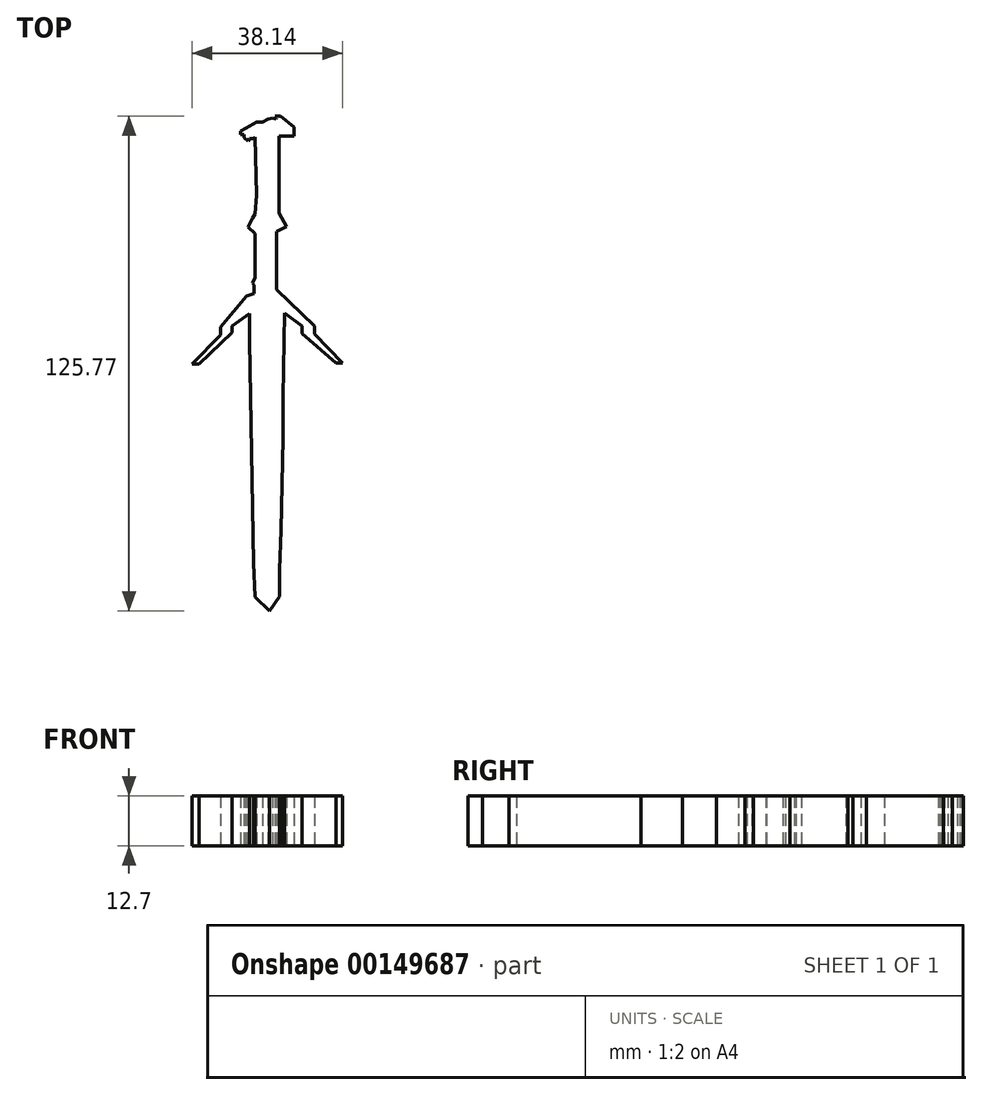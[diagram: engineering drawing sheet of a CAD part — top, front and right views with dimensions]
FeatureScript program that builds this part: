
annotation { "Feature Type Name" : "Feature", "Feature Type Description" : "" }
export const myFeature = defineFeature(function(context is Context, id is Id, definition is map)
    precondition{}
    {
        {
            var Q0;
            Q0=qCreatedBy(makeId("Top.planeOp"),FACE);
            var sketch = newSketch(context, id + "F0", { "sketchPlane" : qUnion([Q0])});
            skLineSegment(sketch, "E0", {"start": v(5, 59.14) * mm, "end": v(8.47, 56.32) * mm});
            skLineSegment(sketch, "E1", {"start": v(8.47, 56.32) * mm, "end": v(8.47, 54.07) * mm});
            skLineSegment(sketch, "E2", {"start": v(8.47, 54.07) * mm, "end": v(4.65, 54.07) * mm});
            skLineSegment(sketch, "E3", {"start": v(4.65, 54.07) * mm, "end": v(4.65, 50.16) * mm});
            skLineSegment(sketch, "E4", {"start": v(4.65, 50.16) * mm, "end": v(4.65, 34.5) * mm});
            skLineSegment(sketch, "E5", {"start": v(4.65, 34.5) * mm, "end": v(6.46, 31.1) * mm});
            skLineSegment(sketch, "E6", {"start": v(6.46, 31.1) * mm, "end": v(4.01, 29.8) * mm});
            skLineSegment(sketch, "E7", {"start": v(4.01, 29.8) * mm, "end": v(4.01, 15.05) * mm});
            skLineSegment(sketch, "E8", {"start": v(4.01, 15.05) * mm, "end": v(13.64, 5.8) * mm});
            skLineSegment(sketch, "E9", {"start": v(13.64, 5.8) * mm, "end": v(13.64, 3.72) * mm});
            skLineSegment(sketch, "E10", {"start": v(13.64, 3.72) * mm, "end": v(20.67, -3.6) * mm});
            skLineSegment(sketch, "E11", {"start": v(20.67, -3.6) * mm, "end": v(19.05, -3.6) * mm});
            skLineSegment(sketch, "E12", {"start": v(19.05, -3.6) * mm, "end": v(10.5, 3.85) * mm});
            skLineSegment(sketch, "E13", {"start": v(10.5, 3.85) * mm, "end": v(10.5, 5.74) * mm});
            skLineSegment(sketch, "E14", {"start": v(10.5, 5.74) * mm, "end": v(6.06, 9.12) * mm});
            skLineSegment(sketch, "E15", {"start": v(6.06, 9.12) * mm, "end": v(5.58, -12.24) * mm});
            skLineSegment(sketch, "E16", {"start": v(5.58, -12.24) * mm, "end": v(5.58, -22.8) * mm});
            skLineSegment(sketch, "E17", {"start": v(5.58, -22.8) * mm, "end": v(5.08, -46.04) * mm});
            skLineSegment(sketch, "E18", {"start": v(5.08, -46.04) * mm, "end": v(4.78, -56.27) * mm});
            skLineSegment(sketch, "E19", {"start": v(4.78, -56.27) * mm, "end": v(4.78, -62.97) * mm});
            skLineSegment(sketch, "E20", {"start": v(4.78, -62.97) * mm, "end": v(2.17, -66.63) * mm});
            skLineSegment(sketch, "E21", {"start": v(2.17, -66.63) * mm, "end": v(-1.54, -63.13) * mm});
            skLineSegment(sketch, "E22", {"start": v(-1.54, -63.13) * mm, "end": v(-1.9, -54.4) * mm});
            skLineSegment(sketch, "E23", {"start": v(-1.9, -54.4) * mm, "end": v(-2.52, -19.79) * mm});
            skLineSegment(sketch, "E24", {"start": v(-2.52, -19.79) * mm, "end": v(-2.91, 2) * mm});
            skLineSegment(sketch, "E25", {"start": v(-2.91, 2) * mm, "end": v(-2.91, 8.95) * mm});
            skLineSegment(sketch, "E26", {"start": v(-2.91, 8.95) * mm, "end": v(-7.36, 5.73) * mm});
            skLineSegment(sketch, "E27", {"start": v(-7.36, 5.73) * mm, "end": v(-7.36, 4.13) * mm});
            skLineSegment(sketch, "E28", {"start": v(-7.36, 4.13) * mm, "end": v(-15.75, -3.89) * mm});
            skLineSegment(sketch, "E29", {"start": v(-15.75, -3.89) * mm, "end": v(-17.47, -3.89) * mm});
            skLineSegment(sketch, "E30", {"start": v(-17.47, -3.89) * mm, "end": v(-10.28, 3.46) * mm});
            skLineSegment(sketch, "E31", {"start": v(-10.28, 3.46) * mm, "end": v(-10.28, 5.47) * mm});
            skLineSegment(sketch, "E32", {"start": v(-10.28, 5.47) * mm, "end": v(-3.65, 13.32) * mm});
            skLineSegment(sketch, "E33", {"start": v(-3.65, 13.32) * mm, "end": v(-1.75, 14.01) * mm});
            skLineSegment(sketch, "E34", {"start": v(-1.75, 14.01) * mm, "end": v(-1.75, 16.24) * mm});
            skLineSegment(sketch, "E35", {"start": v(-1.75, 16.24) * mm, "end": v(-2.1, 16.68) * mm});
            skLineSegment(sketch, "E36", {"start": v(-2.1, 16.68) * mm, "end": v(-1.51, 18.04) * mm});
            skLineSegment(sketch, "E37", {"start": v(-1.51, 18.04) * mm, "end": v(-1.51, 29.28) * mm});
            skLineSegment(sketch, "E38", {"start": v(-1.51, 29.28) * mm, "end": v(-3.28, 30.87) * mm});
            skLineSegment(sketch, "E39", {"start": v(-3.28, 30.87) * mm, "end": v(-2.16, 33.14) * mm});
            skLineSegment(sketch, "E40", {"start": v(-2.16, 33.14) * mm, "end": v(-1.47, 34.27) * mm});
            skLineSegment(sketch, "E41", {"start": v(-1.47, 34.27) * mm, "end": v(-1.06, 39.05) * mm});
            skLineSegment(sketch, "E42", {"start": v(-1.06, 39.05) * mm, "end": v(-1.44, 51.93) * mm});
            skLineSegment(sketch, "E43", {"start": v(-1.44, 51.93) * mm, "end": v(-1.5, 53.8) * mm});
            skLineSegment(sketch, "E44", {"start": v(-1.5, 53.8) * mm, "end": v(-1.97, 53.37) * mm});
            skLineSegment(sketch, "E45", {"start": v(-1.97, 53.37) * mm, "end": v(-2.85, 53.37) * mm});
            skLineSegment(sketch, "E46", {"start": v(-2.85, 53.37) * mm, "end": v(-3.3, 52.8) * mm});
            skLineSegment(sketch, "E47", {"start": v(-3.3, 52.8) * mm, "end": v(-4.32, 53.58) * mm});
            skLineSegment(sketch, "E48", {"start": v(-4.32, 53.58) * mm, "end": v(-4.32, 54.38) * mm});
            skLineSegment(sketch, "E49", {"start": v(-4.32, 54.38) * mm, "end": v(-5.14, 54.38) * mm});
            skLineSegment(sketch, "E50", {"start": v(-5.14, 54.38) * mm, "end": v(-5.14, 55.23) * mm});
            skLineSegment(sketch, "E51", {"start": v(-5.14, 55.23) * mm, "end": v(-3.73, 56.03) * mm});
            skLineSegment(sketch, "E52", {"start": v(-3.73, 56.03) * mm, "end": v(-1.06, 57.64) * mm});
            skLineSegment(sketch, "E53", {"start": v(-1.06, 57.64) * mm, "end": v(0, 57.64) * mm});
            skLineSegment(sketch, "E54", {"start": v(0, 57.64) * mm, "end": v(0.44, 57.64) * mm});
            skLineSegment(sketch, "E55", {"start": v(0.44, 57.64) * mm, "end": v(1.81, 58.32) * mm});
            skLineSegment(sketch, "E56", {"start": v(1.81, 58.32) * mm, "end": v(3, 58.63) * mm});
            skLineSegment(sketch, "E57", {"start": v(3, 58.63) * mm, "end": v(3.9, 58.3) * mm});
            skLineSegment(sketch, "E58", {"start": v(3.9, 58.3) * mm, "end": v(4.01, 58.58) * mm});
            skLineSegment(sketch, "E59", {"start": v(4.01, 58.58) * mm, "end": v(3.58, 59.1) * mm});
            skLineSegment(sketch, "E60", {"start": v(5, 59.14) * mm, "end": v(3.58, 59.1) * mm});
            skSolve(sketch);
        }
        {
            var Q0;
            Q0 = qSketchRegion(id + "F0", true);
            extrude(context, id + "F1", {"entities" : qUnion([Q0]), "depth" : 12.7 * mm});
        }
    });
